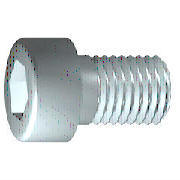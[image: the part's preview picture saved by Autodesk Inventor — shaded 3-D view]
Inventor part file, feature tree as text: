
AUTODESK INVENTOR PART (.ipt)
format: ipt  version: 2020 (Build 240168000, 168)  size: 199,680 bytes
history: native  units: mm (DEFAULTED — no unit token found)
features: sketch x2, other x1, extrude x1, plane x1, fillet x1
ambient origin geometry x7: Origin, YZ Plane, XY Plane, X Axis, Y Axis, Z Axis, Center Point
bodies: Solid1 (feature_tree)
feature tree (6):
  other  "Körper"
  extrude  "Loch"  Depth=3.0mm
  plane  "Work Plane1"
  fillet  "Fillet2"  Radius=3.0mm
  sketch  "Skizze1"  dims[d1=6.5mm d2=0.306825mm d3=3.0mm]
  sketch  "Skizze2"  dims[d4=1.3mm d5=60.0deg d6=3.0mm d7=3.0mm d8=2.886751mm d9=5.5mm d10=90.0deg d11=10.0mm d12=0.0mm d13=6.5mm d14=0.0mm d15=0.306725mm d16=0.306725mm d17=0.3mm d19=0.0mm d26=8.0mm d27=45.0deg d28=0.0mm d29=0.0mm d30=0.1mm]
